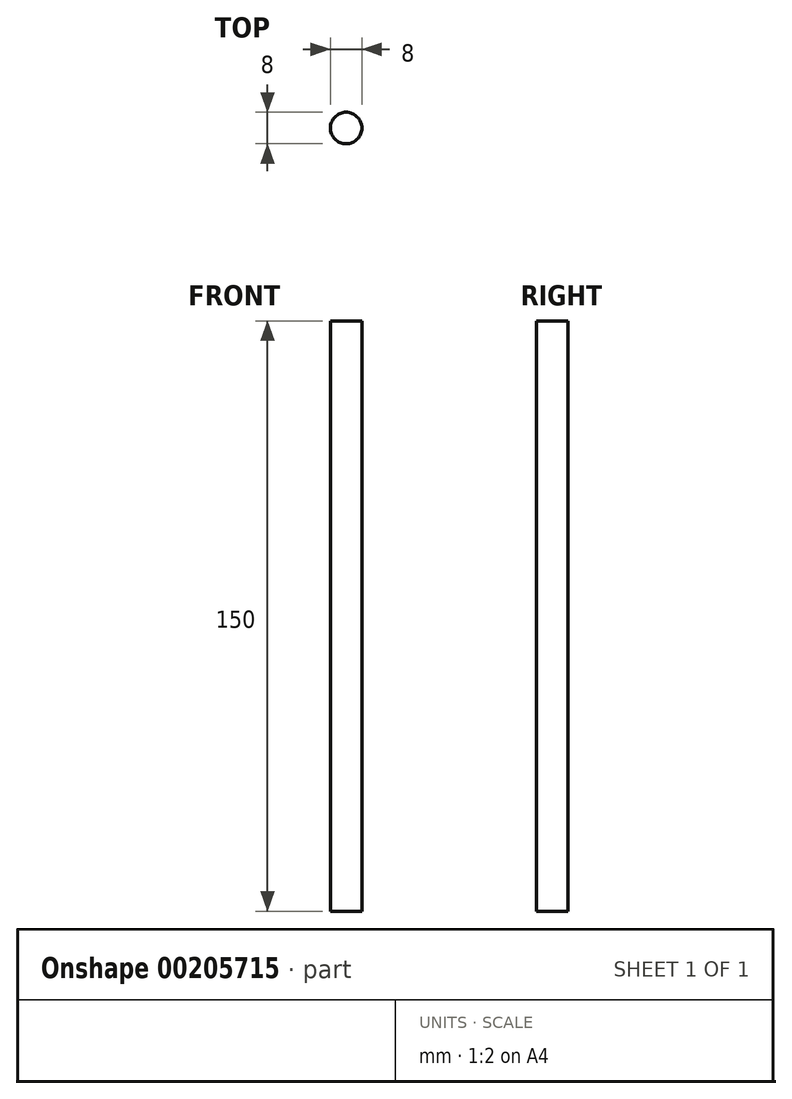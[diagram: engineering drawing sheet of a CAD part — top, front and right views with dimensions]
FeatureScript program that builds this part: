
annotation { "Feature Type Name" : "Feature", "Feature Type Description" : "" }
export const myFeature = defineFeature(function(context is Context, id is Id, definition is map)
    precondition{}
    {
        {
            var Q0;
            Q0=qCreatedBy(makeId("Top.planeOp"),FACE);
            var sketch = newSketch(context, id + "F0", { "sketchPlane" : qUnion([Q0])});
            skCircle(sketch, "E0", {"center": v(0, 0) * mm, "radius": 4 * mm});
            skSolve(sketch);
        }
        {
            var Q0;
            Q0 = qSketchRegion(id + "F0", true);
            extrude(context, id + "F1", {"entities" : qUnion([Q0]), "depth" : 150 * mm});
        }
    });
